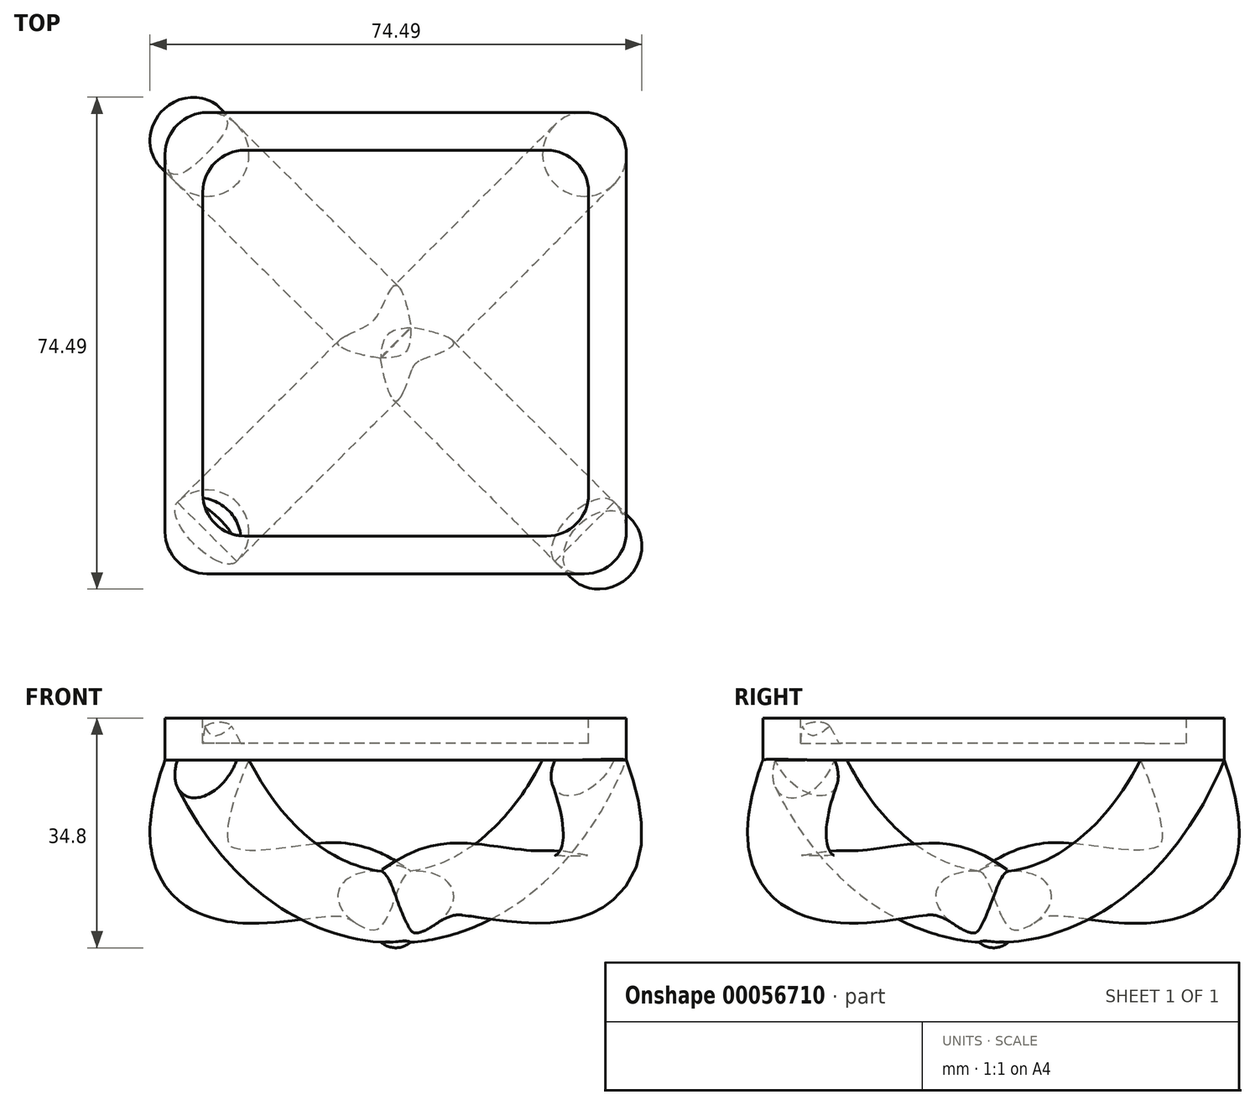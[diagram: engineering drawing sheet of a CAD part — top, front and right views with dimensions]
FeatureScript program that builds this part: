
annotation { "Feature Type Name" : "Feature", "Feature Type Description" : "" }
export const myFeature = defineFeature(function(context is Context, id is Id, definition is map)
    precondition{}
    {
        {
            var Q0;
            Q0=qCreatedBy(makeId("Top.planeOp"),FACE);
            var sketch = newSketch(context, id + "F0", { "sketchPlane" : qUnion([Q0])});
            skLineSegment(sketch, "E0.rect.bottom", {"start": v(34.93, 34.93) * mm, "end": v(-34.93, 34.92) * mm});
            skLineSegment(sketch, "E0.rect.top", {"start": v(34.93, -34.92) * mm, "end": v(-34.93, -34.93) * mm});
            skLineSegment(sketch, "E0.rect.left", {"start": v(34.93, 34.93) * mm, "end": v(34.93, -34.92) * mm});
            skLineSegment(sketch, "E0.rect.right", {"start": v(-34.93, 34.92) * mm, "end": v(-34.93, -34.93) * mm});
            skPoint(sketch, "E0.rect.middle", {"position": v(0, 0) * mm});
            skSolve(sketch);
        }
        {
            var Q0;
            Q0 = qSketchRegion(id + "F0", true);
            extrude(context, id + "F1", {"entities" : qUnion([Q0]), "depth" : 6.35 * mm});
        }
        {
            var Q0;
            Q0=makeQuery(id+"F1.opExtrude","CAP_FACE",FACE,{"disambiguationData":[OSD([sQuery(id+"F0.wireOp",EDGE,"E0.rect.bottom"),sQuery(id+"F0.wireOp",EDGE,"E0.rect.top"),sQuery(id+"F0.wireOp",EDGE,"E0.rect.left"),sQuery(id+"F0.wireOp",EDGE,"E0.rect.right")])],"isStart":false});
            var sketch = newSketch(context, id + "F2", { "sketchPlane" : qUnion([Q0])});
            skLineSegment(sketch, "E1.rect.bottom", {"start": v(22.86, 29.21) * mm, "end": v(-22.86, 29.21) * mm});
            skLineSegment(sketch, "E1.rect.top", {"start": v(22.86, -29.2) * mm, "end": v(-22.86, -29.2) * mm});
            skLineSegment(sketch, "E1.rect.left", {"start": v(29.21, 22.86) * mm, "end": v(29.21, -22.86) * mm});
            skLineSegment(sketch, "E1.rect.right", {"start": v(-29.21, 22.86) * mm, "end": v(-29.21, -22.86) * mm});
            skPoint(sketch, "E1.rect.middle", {"position": v(0, 0) * mm});
            skPoint(sketch, "E2.visualSharp", {"position": v(-29.2, 29.21) * mm});
            skArc(sketch, "E2.filletArc", {"start": v(-22.86, 29.21) * mm, "mid": v(-27.35, 27.35) * mm, "end": v(-29.21, 22.86) * mm});
            skPoint(sketch, "E3.visualSharp", {"position": v(29.21, 29.21) * mm});
            skArc(sketch, "E3.filletArc", {"start": v(29.21, 22.86) * mm, "mid": v(27.35, 27.35) * mm, "end": v(22.86, 29.21) * mm});
            skPoint(sketch, "E4.visualSharp", {"position": v(29.21, -29.2) * mm});
            skArc(sketch, "E4.filletArc", {"start": v(22.86, -29.21) * mm, "mid": v(27.35, -27.35) * mm, "end": v(29.21, -22.86) * mm});
            skPoint(sketch, "E5.visualSharp", {"position": v(-29.21, -29.2) * mm});
            skArc(sketch, "E5.filletArc", {"start": v(-29.21, -22.86) * mm, "mid": v(-27.35, -27.35) * mm, "end": v(-22.86, -29.21) * mm});
            skSolve(sketch);
        }
        {
            var Q0;
            Q0=makeQuery(id+"F2.imprint","IMPRINT",FACE,{"disambiguationData":[TD([[makeQuery(id+"F2.imprint","IMPRINT",EDGE,{"derivedFrom":sQuery(id+"F2.wireOp",EDGE,"E1.rect.bottom")}),1.0]])]});
            extrude(context, id + "F3", {"entities" : qUnion([Q0]), "operationType" : NewBodyOperationType.REMOVE, "oppositeDirection" : true, "depth" : 3.8 * mm});
        }
        {
            var Q0;
            Q0=makeQuery(id+"F1.opExtrude","SWEPT_EDGE",EDGE,{"disambiguationData":[OSD([sQuery(id+"F0.wireOp",EDGE,"E0.rect.top"),sQuery(id+"F0.wireOp",EDGE,"E0.rect.left")])]});
            var Q1;
            Q1=makeQuery(id+"F1.opExtrude","SWEPT_EDGE",EDGE,{"disambiguationData":[OSD([sQuery(id+"F0.wireOp",EDGE,"E0.rect.top"),sQuery(id+"F0.wireOp",EDGE,"E0.rect.right")])]});
            var Q2;
            Q2=makeQuery(id+"F1.opExtrude","SWEPT_EDGE",EDGE,{"disambiguationData":[OSD([sQuery(id+"F0.wireOp",EDGE,"E0.rect.bottom"),sQuery(id+"F0.wireOp",EDGE,"E0.rect.left")])]});
            var Q3;
            Q3=makeQuery(id+"F1.opExtrude","SWEPT_EDGE",EDGE,{"disambiguationData":[OSD([sQuery(id+"F0.wireOp",EDGE,"E0.rect.bottom"),sQuery(id+"F0.wireOp",EDGE,"E0.rect.right")])]});
            fillet(context, id + "F4", {"entities" : qUnion([Q0, Q1, Q2, Q3]), "radius" : 6.35 * mm, "tangentPropagation" : true, "allowEdgeOverflow" : false});
        }
        {
            var Q0;
            Q0=makeQuery(id+"F1.opExtrude","CAP_FACE",FACE,{"disambiguationData":[OSD([sQuery(id+"F0.wireOp",EDGE,"E0.rect.bottom"),sQuery(id+"F0.wireOp",EDGE,"E0.rect.top"),sQuery(id+"F0.wireOp",EDGE,"E0.rect.left"),sQuery(id+"F0.wireOp",EDGE,"E0.rect.right")])],"isStart":true});
            var sketch = newSketch(context, id + "F5", { "sketchPlane" : qUnion([Q0])});
            skCircle(sketch, "E6", {"center": v(28.58, 28.57) * mm, "radius": 6.35 * mm});
            skCircle(sketch, "E7", {"center": v(28.58, -28.58) * mm, "radius": 6.35 * mm});
            skCircle(sketch, "E8", {"center": v(-28.58, -28.57) * mm, "radius": 6.35 * mm});
            skCircle(sketch, "E9", {"center": v(-28.57, 28.58) * mm, "radius": 6.35 * mm});
            skLineSegment(sketch, "E10", {"start": v(-28.58, -28.57) * mm, "end": v(28.58, 28.57) * mm});
            skLineSegment(sketch, "E11", {"start": v(-28.57, 28.57) * mm, "end": v(28.57, -28.57) * mm});
            skSolve(sketch);
        }
        {
            var Q0;
            Q0=sQuery(id+"F5.wireOp",EDGE,"E10");
            var Q1;
            Q1=qCreatedBy(makeId("Front.planeOp"),FACE);
            cPlane(context, id + "F6", {"entities" : qUnion([Q0, Q1]), "cplaneType" : CPlaneType.LINE_ANGLE, "offset" : 152.4 * mm, "angle" : 0 * degree, "width" : 152.4 * mm, "height" : 152.4 * mm});
        }
        {
            var Q0;
            Q0=sQuery(id+"F5.wireOp",EDGE,"E11");
            var Q1;
            Q1=qCreatedBy(makeId("Front.planeOp"),FACE);
            cPlane(context, id + "F7", {"entities" : qUnion([Q0, Q1]), "cplaneType" : CPlaneType.LINE_ANGLE, "offset" : 152.4 * mm, "angle" : 0 * degree, "width" : 152.4 * mm, "height" : 152.4 * mm});
        }
        {
            var Q0;
            Q0=qCreatedBy(id+"F6.planeOp",FACE);
            var sketch = newSketch(context, id + "F8", { "sketchPlane" : qUnion([Q0])});
            skPoint(sketch, "E12", {"position": v(0, -22.23) * mm});
            skFitSpline(sketch, "E13", {"points": [v(-40.41, 0) * mm, v(-34.64, -18.82) * mm, v(-11.47, -18.31) * mm, v(0, -22.23) * mm], "startDerivative": vector(-68.9, -121.97) * mm, "endDerivative": vector(34.46, -17.82) * mm});
            skFitSpline(sketch, "E14.MirrorCS", {"points": [v(40.41, 0) * mm, v(34.64, -18.82) * mm, v(11.47, -18.31) * mm, v(0, -22.23) * mm], "startDerivative": vector(68.9, -121.97) * mm, "endDerivative": vector(-34.46, -17.82) * mm});
            skFitSpline(sketch, "E15.MirrorCS", {"points": [v(-40.41, 0) * mm, v(-34.64, -18.82) * mm, v(-11.47, -18.31) * mm, v(0, -22.23) * mm], "startDerivative": vector(-68.9, -121.97) * mm, "endDerivative": vector(34.46, -17.82) * mm});
            skSolve(sketch);
        }
        {
            var Q0;
            Q0=qCreatedBy(id+"F7.planeOp",FACE);
            var sketch = newSketch(context, id + "F9", { "sketchPlane" : qUnion([Q0])});
            skPoint(sketch, "E16", {"position": v(0, -22.23) * mm});
            skArc(sketch, "E17", {"start": v(-40.41, 0) * mm, "mid": v(0, -22.23) * mm, "end": v(40.41, 0) * mm});
            skSolve(sketch);
        }
        {
            var Q0;
            {var subQ0=sQuery(id+"F5.wireOp",EDGE,"E8");var subQ1=makeQuery(id+"F5.imprint","INTERSECT",VERTEX,{"derivedFrom":[makeQuery(id+"F1.opExtrude","CAP_EDGE",EDGE,{"disambiguationData":[OSD([sQuery(id+"F0.wireOp",EDGE,"E0.rect.right")])],"isStart":true}),subQ0]});Q0=makeQuery(id+"F5.imprint","IMPRINT",FACE,{"disambiguationData":[TD([[makeQuery(id+"F5.imprint","IMPRINT",EDGE,{"disambiguationData":[TD([[subQ1,1.0]])],"derivedFrom":subQ0}),1.0]])]});}
            var Q1;
            Q1=sQuery(id+"F8.wireOp",EDGE,"E14.MirrorCS");
            var Q2;
            Q2=sQuery(id+"F8.wireOp",EDGE,"E13");
            sweep(context, id + "F10", {"profiles" : qUnion([Q0]), "path" : qUnion([Q1, Q2])});
        }
        {
            var Q0;
            Q0=makeQuery(id+"F1.opExtrude","CAP_FACE",FACE,{"disambiguationData":[OSD([sQuery(id+"F0.wireOp",EDGE,"E0.rect.bottom"),sQuery(id+"F0.wireOp",EDGE,"E0.rect.top"),sQuery(id+"F0.wireOp",EDGE,"E0.rect.left"),sQuery(id+"F0.wireOp",EDGE,"E0.rect.right")])],"isStart":true});
            var sketch = newSketch(context, id + "F11", { "sketchPlane" : qUnion([Q0])});
            skCircle(sketch, "E18", {"center": v(-28.57, 28.58) * mm, "radius": 6.35 * mm});
            skCircle(sketch, "E19", {"center": v(28.58, -28.58) * mm, "radius": 6.35 * mm});
            skSolve(sketch);
        }
        {
            var Q0;
            {var subQ0=sQuery(id+"F11.wireOp",EDGE,"E19");var subQ1=makeQuery(id+"F11.imprint","INTERSECT",VERTEX,{"derivedFrom":[makeQuery(id+"F1.opExtrude","CAP_EDGE",EDGE,{"disambiguationData":[OSD([sQuery(id+"F0.wireOp",EDGE,"E0.rect.bottom")])],"isStart":true}),subQ0]});Q0=makeQuery(id+"F11.imprint","IMPRINT",FACE,{"disambiguationData":[TD([[makeQuery(id+"F11.imprint","IMPRINT",EDGE,{"disambiguationData":[TD([[subQ1,1.0]])],"derivedFrom":subQ0}),1.0]])]});}
            var Q1;
            Q1=sQuery(id+"F9.wireOp",EDGE,"E17");
            sweep(context, id + "F12", {"operationType" : NewBodyOperationType.ADD, "profiles" : qUnion([Q0]), "path" : qUnion([Q1])});
        }
    });
